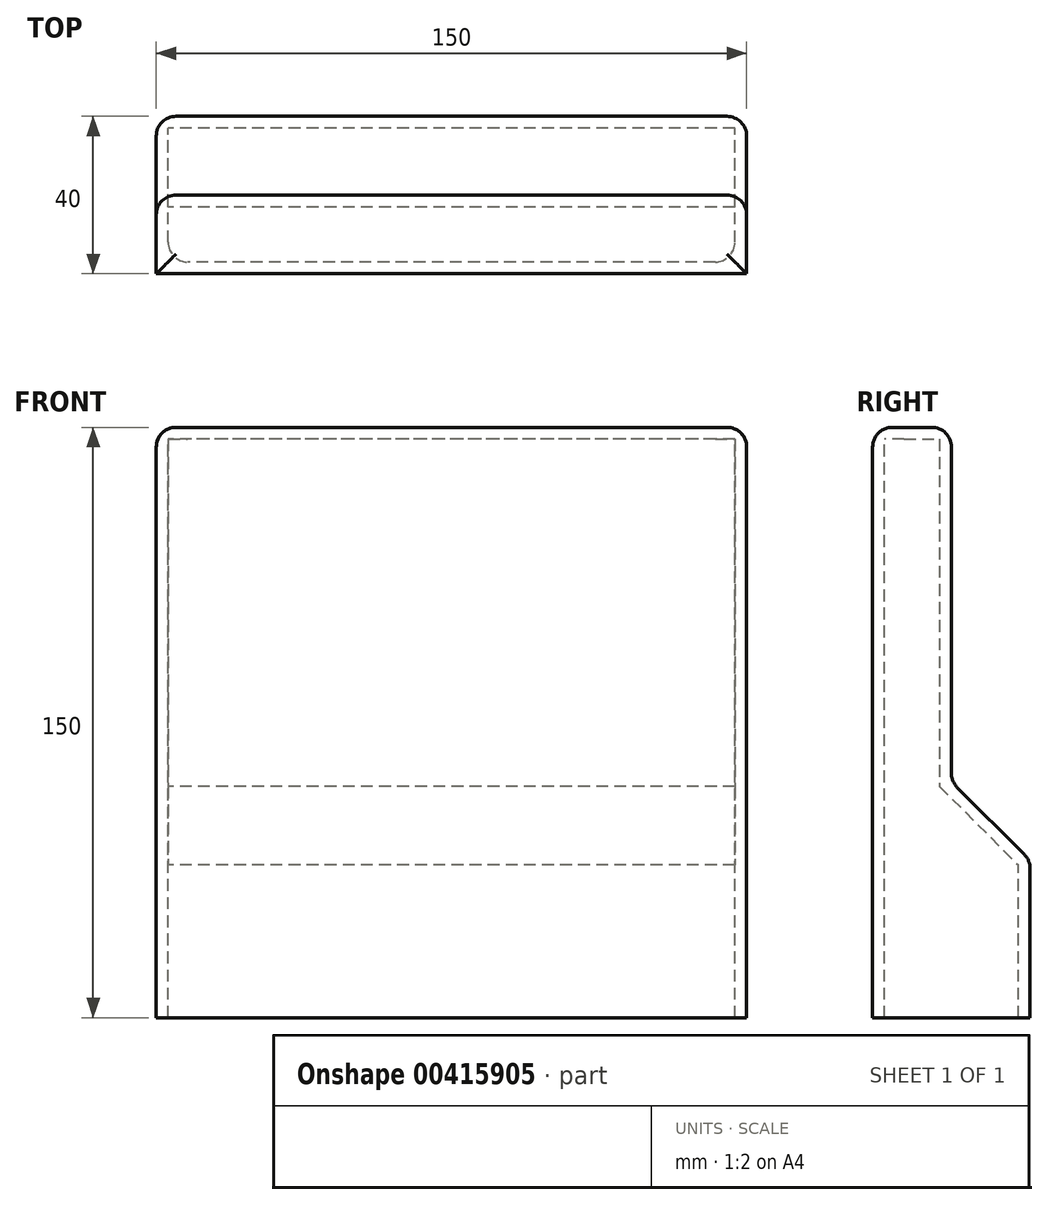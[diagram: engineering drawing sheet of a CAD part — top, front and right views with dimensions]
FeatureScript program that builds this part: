
annotation { "Feature Type Name" : "Feature", "Feature Type Description" : "" }
export const myFeature = defineFeature(function(context is Context, id is Id, definition is map)
    precondition{}
    {
        {
            assignVariable(context, id + "F0", {"name" : "Width", "anyValue" : 150});
        }
        {
            assignVariable(context, id + "F1", {"name" : "WallThickness", "anyValue" : 3});
        }
        {
            var Q0;
            Q0=qCreatedBy(makeId("Right.planeOp"),FACE);
            var sketch = newSketch(context, id + "F2", { "sketchPlane" : qUnion([Q0])});
            skLineSegment(sketch, "E0", {"start": v(0, 0) * mm, "end": v(0, 75) * mm});
            skLineSegment(sketch, "E1", {"start": v(0, 75) * mm, "end": v(20, 75) * mm});
            skLineSegment(sketch, "E2", {"start": v(20, 75) * mm, "end": v(20, -15) * mm});
            skLineSegment(sketch, "E3", {"start": v(0, 0) * mm, "end": v(0, -75) * mm});
            skLineSegment(sketch, "E4", {"start": v(0, -75) * mm, "end": v(40, -75) * mm});
            skLineSegment(sketch, "E5", {"start": v(40, -75) * mm, "end": v(40, -35) * mm});
            skLineSegment(sketch, "E6", {"start": v(20, -15) * mm, "end": v(40, -35) * mm});
            skSolve(sketch);
        }
        {
            var Q0;
            Q0 = qSketchRegion(id + "F2", true);
            extrude(context, id + "F3", {"entities" : qUnion([Q0]), "endBound" : BoundingType.SYMMETRIC, "depth" : (getVariable(context, 'Width')) * mm});
        }
        {
            var Q0;
            Q0=makeQuery(id+"F3.opExtrude","SWEPT_FACE",FACE,{"disambiguationData":[OSD([sQuery(id+"F2.wireOp",EDGE,"E4")])]});
            shell(context, id + "F4", {"entities" : qUnion([Q0]), "thickness" : (getVariable(context, 'WallThickness')) * mm});
        }
        {
            var Q0;
            {var subQ0=sQuery(id+"F2.wireOp",EDGE,"E3");var subQ1=sQuery(id+"F2.wireOp",EDGE,"E0");Q0=makeQuery(id+"F4.opShell","OFFSET_EDGE",EDGE,{"disambiguationData":[OSD([subQ1,subQ0]),TDD([makeQuery(id+"F3.opExtrude","CAP_EDGE",EDGE,{"disambiguationData":[OSD([subQ1,subQ0])],"isStart":false})])]});}
            var Q1;
            {var subQ0=sQuery(id+"F2.wireOp",EDGE,"E3");var subQ1=sQuery(id+"F2.wireOp",EDGE,"E0");Q1=makeQuery(id+"F4.opShell","OFFSET_EDGE",EDGE,{"disambiguationData":[OSD([subQ1,subQ0]),TDD([makeQuery(id+"F3.opExtrude","CAP_EDGE",EDGE,{"disambiguationData":[OSD([subQ1,subQ0])],"isStart":true})])]});}
            var Q2;
            Q2=makeQuery(id+"F3.opExtrude","CAP_EDGE",EDGE,{"disambiguationData":[OSD([sQuery(id+"F2.wireOp",EDGE,"E1")])],"isStart":true});
            var Q3;
            Q3=makeQuery(id+"F3.opExtrude","CAP_EDGE",EDGE,{"disambiguationData":[OSD([sQuery(id+"F2.wireOp",EDGE,"E2")])],"isStart":true});
            var Q4;
            Q4=makeQuery(id+"F3.opExtrude","CAP_EDGE",EDGE,{"disambiguationData":[OSD([sQuery(id+"F2.wireOp",EDGE,"E6")])],"isStart":true});
            var Q5;
            Q5=makeQuery(id+"F3.opExtrude","CAP_EDGE",EDGE,{"disambiguationData":[OSD([sQuery(id+"F2.wireOp",EDGE,"E5")])],"isStart":true});
            var Q6;
            Q6=makeQuery(id+"F3.opExtrude","SWEPT_EDGE",EDGE,{"disambiguationData":[OSD([sQuery(id+"F2.wireOp",EDGE,"E1"),sQuery(id+"F2.wireOp",EDGE,"E2")])]});
            var Q7;
            Q7=makeQuery(id+"F3.opExtrude","SWEPT_FACE",FACE,{"disambiguationData":[OSD([sQuery(id+"F2.wireOp",EDGE,"E1")])]});
            var Q8;
            Q8=makeQuery(id+"F3.opExtrude","CAP_EDGE",EDGE,{"disambiguationData":[OSD([sQuery(id+"F2.wireOp",EDGE,"E2")])],"isStart":false});
            var Q9;
            Q9=makeQuery(id+"F3.opExtrude","CAP_EDGE",EDGE,{"disambiguationData":[OSD([sQuery(id+"F2.wireOp",EDGE,"E6")])],"isStart":false});
            var Q10;
            Q10=makeQuery(id+"F3.opExtrude","CAP_EDGE",EDGE,{"disambiguationData":[OSD([sQuery(id+"F2.wireOp",EDGE,"E5")])],"isStart":false});
            var Q11;
            Q11=makeQuery(id+"F3.opExtrude","SWEPT_EDGE",EDGE,{"disambiguationData":[OSD([sQuery(id+"F2.wireOp",EDGE,"E5"),sQuery(id+"F2.wireOp",EDGE,"E6")])]});
            var Q12;
            Q12=makeQuery(id+"F3.opExtrude","SWEPT_EDGE",EDGE,{"disambiguationData":[OSD([sQuery(id+"F2.wireOp",EDGE,"E2"),sQuery(id+"F2.wireOp",EDGE,"E6")])]});
            fillet(context, id + "F5", {"entities" : qUnion([Q0, Q1, Q2, Q3, Q4, Q5, Q6, Q7, Q8, Q9, Q10, Q11, Q12]), "radius" : 5 * mm, "tangentPropagation" : true, "allowEdgeOverflow" : false});
        }
    });
